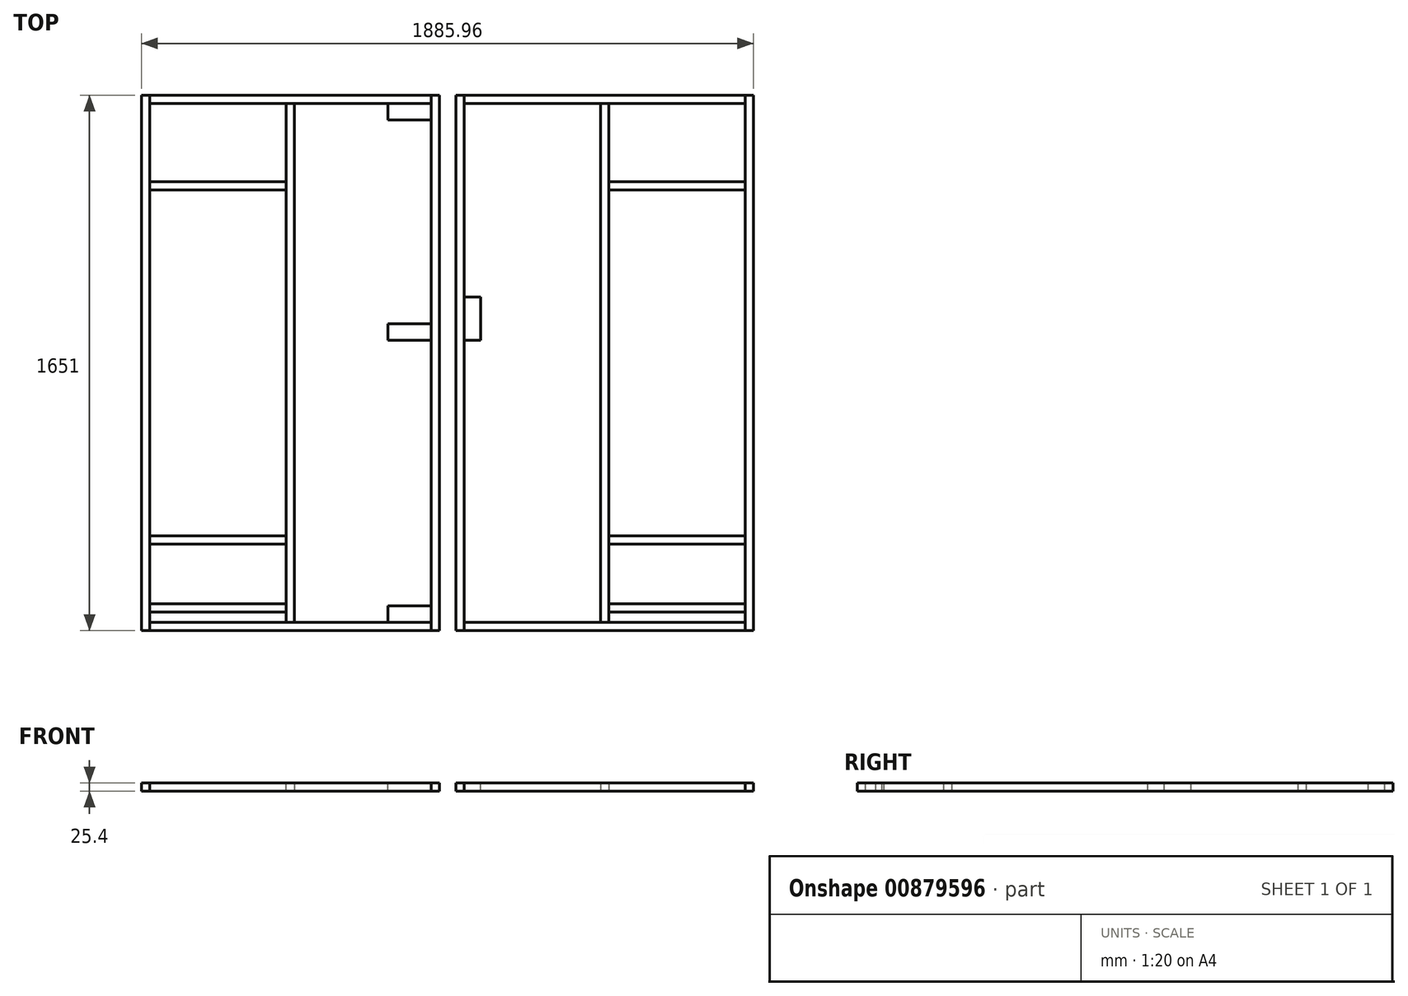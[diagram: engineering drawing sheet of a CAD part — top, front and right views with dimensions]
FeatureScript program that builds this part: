
annotation { "Feature Type Name" : "Feature", "Feature Type Description" : "" }
export const myFeature = defineFeature(function(context is Context, id is Id, definition is map)
    precondition{}
    {
        {
            var Q0;
            Q0=qCreatedBy(makeId("Top.planeOp"),FACE);
            var sketch = newSketch(context, id + "F0", { "sketchPlane" : qUnion([Q0])});
            skLineSegment(sketch, "E0.bottom", {"start": v(0, 0) * mm, "end": v(25.4, 0) * mm});
            skLineSegment(sketch, "E0.top", {"start": v(0, -1651) * mm, "end": v(25.4, -1651) * mm});
            skLineSegment(sketch, "E0.left", {"start": v(0, 0) * mm, "end": v(0, -1651) * mm});
            skLineSegment(sketch, "E0.right", {"start": v(25.4, 0) * mm, "end": v(25.4, -1651) * mm});
            skLineSegment(sketch, "E1.bottom", {"start": v(892.18, 0) * mm, "end": v(917.58, 0) * mm});
            skLineSegment(sketch, "E1.top", {"start": v(892.18, -1651) * mm, "end": v(917.58, -1651) * mm});
            skLineSegment(sketch, "E1.left", {"start": v(892.18, 0) * mm, "end": v(892.18, -1651) * mm});
            skLineSegment(sketch, "E1.right", {"start": v(917.58, 0) * mm, "end": v(917.58, -1651) * mm});
            skLineSegment(sketch, "E2", {"start": v(25.4, 0) * mm, "end": v(892.18, 0) * mm, "construction": true});
            skSolve(sketch);
        }
        {
            var Q0;
            Q0=qSketchRegion(id+"F0",true);
            extrude(context, id + "F1", {"entities" : qUnion([Q0]), "depth" : 25.4 * mm, "offsetDistance" : 25.4 * mm});
        }
        {
            var Q0;
            Q0=makeQuery(id+"F1.opExtrude","SWEPT_FACE",FACE,{"disambiguationData":[OSD([sQuery(id+"F0.wireOp",EDGE,"E0.right")])]});
            var sketch = newSketch(context, id + "F2", { "sketchPlane" : qUnion([Q0])});
            skLineSegment(sketch, "E3.bottom", {"start": v(0, 0) * mm, "end": v(-25.4, 0) * mm});
            skLineSegment(sketch, "E3.top", {"start": v(0, 25.4) * mm, "end": v(-25.4, 25.4) * mm});
            skLineSegment(sketch, "E3.left", {"start": v(0, 0) * mm, "end": v(0, 25.4) * mm});
            skLineSegment(sketch, "E3.right", {"start": v(-25.4, 0) * mm, "end": v(-25.4, 25.4) * mm});
            skLineSegment(sketch, "E4.bottom", {"start": v(-1651, 25.4) * mm, "end": v(-1625.6, 25.4) * mm});
            skLineSegment(sketch, "E4.top", {"start": v(-1651, 0) * mm, "end": v(-1625.6, 0) * mm});
            skLineSegment(sketch, "E4.left", {"start": v(-1651, 25.4) * mm, "end": v(-1651, 0) * mm});
            skLineSegment(sketch, "E4.right", {"start": v(-1625.6, 25.4) * mm, "end": v(-1625.6, 0) * mm});
            skSolve(sketch);
        }
        {
            var Q0;
            Q0=qSketchRegion(id+"F2",true);
            var Q1;
            Q1=makeQuery(id+"F1.opExtrude","SWEPT_FACE",FACE,{"disambiguationData":[OSD([sQuery(id+"F0.wireOp",EDGE,"E1.left")])]});
            extrude(context, id + "F3", {"entities" : qUnion([Q0]), "endBound" : BoundingType.UP_TO_SURFACE, "depth" : 25.4 * mm, "endBoundEntityFace" : qUnion([Q1]), "offsetDistance" : 25.4 * mm});
        }
        {
            var Q0;
            Q0=makeQuery(id+"F3.opExtrude","SWEPT_FACE",FACE,{"disambiguationData":[OSD([sQuery(id+"F2.wireOp",EDGE,"E4.right")])]});
            var sketch = newSketch(context, id + "F4", { "sketchPlane" : qUnion([Q0])});
            skLineSegment(sketch, "E5.bottom", {"start": v(-446.09, 0) * mm, "end": v(-471.49, 0) * mm});
            skLineSegment(sketch, "E5.top", {"start": v(-446.09, 25.4) * mm, "end": v(-471.49, 25.4) * mm});
            skLineSegment(sketch, "E5.left", {"start": v(-446.09, 0) * mm, "end": v(-446.09, 25.4) * mm});
            skLineSegment(sketch, "E5.right", {"start": v(-471.49, 0) * mm, "end": v(-471.49, 25.4) * mm});
            skLineSegment(sketch, "E6", {"start": v(-471.49, 12.7) * mm, "end": v(-892.18, 12.7) * mm, "construction": true});
            skLineSegment(sketch, "E7", {"start": v(-446.09, 12.7) * mm, "end": v(-25.4, 12.7) * mm, "construction": true});
            skSolve(sketch);
        }
        {
            var Q0;
            Q0=qSketchRegion(id+"F4",true);
            var Q1;
            Q1=makeQuery(id+"F3.opExtrude","SWEPT_FACE",FACE,{"disambiguationData":[OSD([sQuery(id+"F2.wireOp",EDGE,"E3.right")])]});
            extrude(context, id + "F5", {"entities" : qUnion([Q0]), "endBound" : BoundingType.UP_TO_SURFACE, "depth" : 25.4 * mm, "endBoundEntityFace" : qUnion([Q1]), "offsetDistance" : 25.4 * mm});
        }
        {
            var Q0;
            Q0=makeQuery(id+"F1.opExtrude","SWEPT_FACE",FACE,{"disambiguationData":[OSD([sQuery(id+"F0.wireOp",EDGE,"E1.left")])]});
            var sketch = newSketch(context, id + "F6", { "sketchPlane" : qUnion([Q0])});
            skLineSegment(sketch, "E8.bottom", {"start": v(266.7, 25.4) * mm, "end": v(292.1, 25.4) * mm});
            skLineSegment(sketch, "E8.top", {"start": v(266.7, 0) * mm, "end": v(292.1, 0) * mm});
            skLineSegment(sketch, "E8.left", {"start": v(266.7, 25.4) * mm, "end": v(266.7, 0) * mm});
            skLineSegment(sketch, "E8.right", {"start": v(292.1, 25.4) * mm, "end": v(292.1, 0) * mm});
            skLineSegment(sketch, "E9.bottom", {"start": v(1593.85, 25.4) * mm, "end": v(1568.45, 25.4) * mm});
            skLineSegment(sketch, "E9.top", {"start": v(1593.85, 0) * mm, "end": v(1568.45, 0) * mm});
            skLineSegment(sketch, "E9.left", {"start": v(1593.85, 25.4) * mm, "end": v(1593.85, 0) * mm});
            skLineSegment(sketch, "E9.right", {"start": v(1568.45, 25.4) * mm, "end": v(1568.45, 0) * mm});
            skLineSegment(sketch, "E10.bottom", {"start": v(1384.3, 25.4) * mm, "end": v(1358.9, 25.4) * mm});
            skLineSegment(sketch, "E10.top", {"start": v(1384.3, 0) * mm, "end": v(1358.9, 0) * mm});
            skLineSegment(sketch, "E10.left", {"start": v(1384.3, 25.4) * mm, "end": v(1384.3, 0) * mm});
            skLineSegment(sketch, "E10.right", {"start": v(1358.9, 25.4) * mm, "end": v(1358.9, 0) * mm});
            skSolve(sketch);
        }
        {
            var Q0;
            Q0=qSketchRegion(id+"F6",true);
            var Q1;
            Q1=makeQuery(id+"F5.opExtrude","SWEPT_FACE",FACE,{"disambiguationData":[OSD([sQuery(id+"F4.wireOp",EDGE,"E5.right")])]});
            extrude(context, id + "F7", {"entities" : qUnion([Q0]), "endBound" : BoundingType.UP_TO_SURFACE, "depth" : 25.4 * mm, "endBoundEntityFace" : qUnion([Q1]), "offsetDistance" : 25.4 * mm});
        }
        {
            var Q0;
            Q0=makeQuery(id+"F1.opExtrude","SWEPT_FACE",FACE,{"disambiguationData":[OSD([sQuery(id+"F0.wireOp",EDGE,"E0.left")])]});
            cPlane(context, id + "F8", {"entities" : qUnion([Q0]), "cplaneType" : CPlaneType.OFFSET, "offset" : 25.4 * mm, "width" : 152.4 * mm, "height" : 152.4 * mm});
        }
        {
            var Q0;
            Q0=makeQuery(id+"F1.opExtrude","SWEPT_BODY",BODY,{"disambiguationData":[OSD([sQuery(id+"F0.wireOp",EDGE,"E0.bottom"),sQuery(id+"F0.wireOp",EDGE,"E0.top"),sQuery(id+"F0.wireOp",EDGE,"E0.left"),sQuery(id+"F0.wireOp",EDGE,"E0.right")])]});
            var Q1;
            Q1=makeQuery(id+"F1.opExtrude","SWEPT_BODY",BODY,{"disambiguationData":[OSD([sQuery(id+"F0.wireOp",EDGE,"E1.bottom"),sQuery(id+"F0.wireOp",EDGE,"E1.top"),sQuery(id+"F0.wireOp",EDGE,"E1.left"),sQuery(id+"F0.wireOp",EDGE,"E1.right")])]});
            var Q2;
            Q2=makeQuery(id+"F7.opExtrude","SWEPT_BODY",BODY,{"disambiguationData":[OSD([sQuery(id+"F6.wireOp",EDGE,"E10.bottom"),sQuery(id+"F6.wireOp",EDGE,"E10.top"),sQuery(id+"F6.wireOp",EDGE,"E10.left"),sQuery(id+"F6.wireOp",EDGE,"E10.right")])]});
            var Q3;
            Q3=makeQuery(id+"F7.opExtrude","SWEPT_BODY",BODY,{"disambiguationData":[OSD([sQuery(id+"F6.wireOp",EDGE,"E9.bottom"),sQuery(id+"F6.wireOp",EDGE,"E9.top"),sQuery(id+"F6.wireOp",EDGE,"E9.left"),sQuery(id+"F6.wireOp",EDGE,"E9.right")])]});
            var Q4;
            Q4=makeQuery(id+"F7.opExtrude","SWEPT_BODY",BODY,{"disambiguationData":[OSD([sQuery(id+"F6.wireOp",EDGE,"E8.bottom"),sQuery(id+"F6.wireOp",EDGE,"E8.top"),sQuery(id+"F6.wireOp",EDGE,"E8.left"),sQuery(id+"F6.wireOp",EDGE,"E8.right")])]});
            var Q5;
            Q5=makeQuery(id+"F5.opExtrude","SWEPT_BODY",BODY,{"disambiguationData":[OSD([sQuery(id+"F4.wireOp",EDGE,"E5.bottom"),sQuery(id+"F4.wireOp",EDGE,"E5.top"),sQuery(id+"F4.wireOp",EDGE,"E5.left"),sQuery(id+"F4.wireOp",EDGE,"E5.right")])]});
            var Q6;
            Q6=makeQuery(id+"F3.opExtrude","SWEPT_BODY",BODY,{"disambiguationData":[OSD([sQuery(id+"F2.wireOp",EDGE,"E4.bottom"),sQuery(id+"F2.wireOp",EDGE,"E4.top"),sQuery(id+"F2.wireOp",EDGE,"E4.left"),sQuery(id+"F2.wireOp",EDGE,"E4.right")])]});
            var Q7;
            Q7=makeQuery(id+"F3.opExtrude","SWEPT_BODY",BODY,{"disambiguationData":[OSD([sQuery(id+"F2.wireOp",EDGE,"E3.bottom"),sQuery(id+"F2.wireOp",EDGE,"E3.top"),sQuery(id+"F2.wireOp",EDGE,"E3.left"),sQuery(id+"F2.wireOp",EDGE,"E3.right")])]});
            var Q8;
            Q8=qCreatedBy(id+"F8.planeOp",FACE);
            mirror(context, id + "F9", {"entities" : qUnion([Q0, Q1, Q2, Q3, Q4, Q5, Q6, Q7]), "mirrorPlane" : qUnion([Q8])});
        }
        {
            var Q0;
            Q0=makeQuery(id+"F3.opExtrude","SWEPT_FACE",FACE,{"disambiguationData":[OSD([sQuery(id+"F2.wireOp",EDGE,"E3.top")])]});
            var sketch = newSketch(context, id + "F10", { "sketchPlane" : qUnion([Q0])});
            skLineSegment(sketch, "E11.bottom", {"start": v(-209.55, -25.4) * mm, "end": v(-76.2, -25.4) * mm});
            skLineSegment(sketch, "E11.top", {"start": v(-209.55, -76.2) * mm, "end": v(-76.2, -76.2) * mm});
            skLineSegment(sketch, "E11.left", {"start": v(-209.55, -25.4) * mm, "end": v(-209.55, -76.2) * mm});
            skLineSegment(sketch, "E11.right", {"start": v(-76.2, -25.4) * mm, "end": v(-76.2, -76.2) * mm});
            skLineSegment(sketch, "E12.bottom", {"start": v(-209.55, -1574.8) * mm, "end": v(-76.2, -1574.8) * mm});
            skLineSegment(sketch, "E12.top", {"start": v(-209.55, -1625.6) * mm, "end": v(-76.2, -1625.6) * mm});
            skLineSegment(sketch, "E12.left", {"start": v(-209.55, -1574.8) * mm, "end": v(-209.55, -1625.6) * mm});
            skLineSegment(sketch, "E12.right", {"start": v(-76.2, -1574.8) * mm, "end": v(-76.2, -1625.6) * mm});
            skLineSegment(sketch, "E13.bottom", {"start": v(-209.55, -704.85) * mm, "end": v(-76.2, -704.85) * mm});
            skLineSegment(sketch, "E13.top", {"start": v(-209.55, -755.65) * mm, "end": v(-76.2, -755.65) * mm});
            skLineSegment(sketch, "E13.left", {"start": v(-209.55, -704.85) * mm, "end": v(-209.55, -755.65) * mm});
            skLineSegment(sketch, "E13.right", {"start": v(-76.2, -704.85) * mm, "end": v(-76.2, -755.65) * mm});
            skLineSegment(sketch, "E14.bottom", {"start": v(25.4, -622.3) * mm, "end": v(76.2, -622.3) * mm});
            skLineSegment(sketch, "E14.top", {"start": v(25.4, -755.65) * mm, "end": v(76.2, -755.65) * mm});
            skLineSegment(sketch, "E14.left", {"start": v(25.4, -622.3) * mm, "end": v(25.4, -755.65) * mm});
            skLineSegment(sketch, "E14.right", {"start": v(76.2, -622.3) * mm, "end": v(76.2, -755.65) * mm});
            skLineSegment(sketch, "E15", {"start": v(-76.2, -755.65) * mm, "end": v(25.4, -755.65) * mm, "construction": true});
            skSolve(sketch);
        }
        {
            var Q0;
            Q0 = qSketchRegion(id + "F10", true);
            extrude(context, id + "F11", {"entities" : qUnion([Q0]), "oppositeDirection" : true, "depth" : 25.4 * mm, "offsetDistance" : 25.4 * mm});
        }
    });
